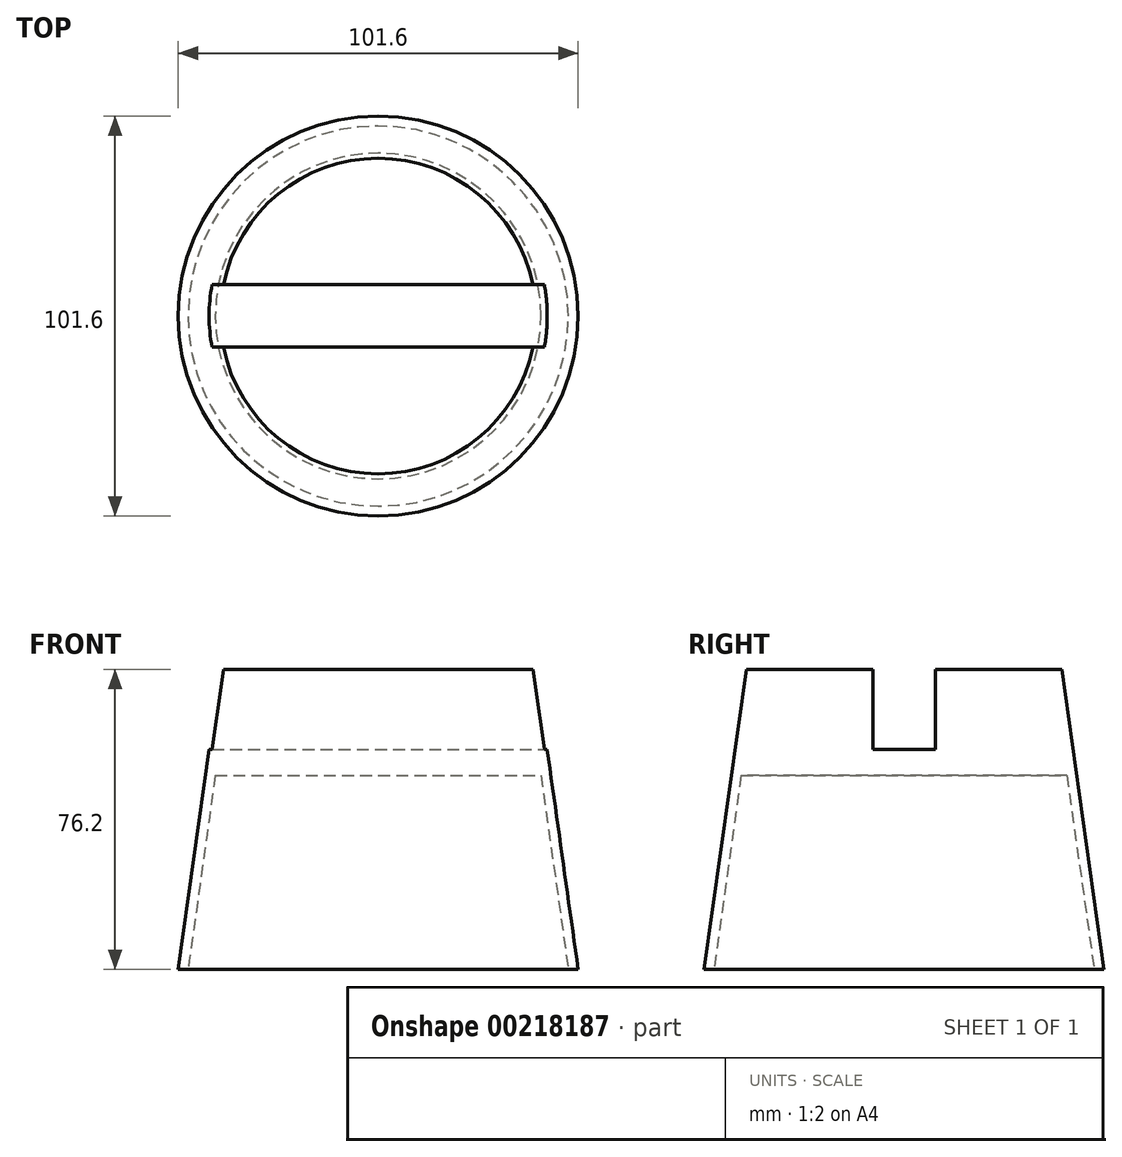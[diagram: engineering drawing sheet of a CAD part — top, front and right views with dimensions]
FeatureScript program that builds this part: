
annotation { "Feature Type Name" : "Feature", "Feature Type Description" : "" }
export const myFeature = defineFeature(function(context is Context, id is Id, definition is map)
    precondition{}
    {
        {
            var Q0;
            Q0=qCreatedBy(makeId("Top.planeOp"),FACE);
            var sketch = newSketch(context, id + "F0", { "sketchPlane" : qUnion([Q0])});
            skCircle(sketch, "E0", {"center": v(0, 0) * mm, "radius": 50.8 * mm});
            skSolve(sketch);
        }
        {
            var Q0;
            Q0 = qSketchRegion(id + "F0", true);
            extrude(context, id + "F1", {"entities" : qUnion([Q0]), "depth" : 76.2 * mm, "hasDraft" : true, "draftAngle" : 8 * degree, "draftPullDirection" : true});
        }
        {
            var Q0;
            Q0=makeQuery(id+"F1.opExtrude","CAP_FACE",FACE,{"disambiguationData":[OSD([sQuery(id+"F0.wireOp",EDGE,"E0")])],"isStart":false});
            var sketch = newSketch(context, id + "F2", { "sketchPlane" : qUnion([Q0])});
            skLineSegment(sketch, "E1.bottom", {"start": v(-63.5, -7.94) * mm, "end": v(63.5, -7.94) * mm});
            skLineSegment(sketch, "E1.top", {"start": v(-63.5, 7.94) * mm, "end": v(63.5, 7.94) * mm});
            skLineSegment(sketch, "E1.left", {"start": v(-63.5, -7.94) * mm, "end": v(-63.5, 7.94) * mm});
            skLineSegment(sketch, "E1.right", {"start": v(63.5, -7.94) * mm, "end": v(63.5, 7.94) * mm});
            skPoint(sketch, "E2", {"position": v(0, 7.94) * mm});
            skPoint(sketch, "E3", {"position": v(0, -7.94) * mm});
            skPoint(sketch, "E4", {"position": v(-63.5, 0) * mm});
            skPoint(sketch, "E5", {"position": v(63.5, 0) * mm});
            skLineSegment(sketch, "E6", {"start": v(40.1, 0) * mm, "end": v(-40.1, 0) * mm, "construction": true});
            skLineSegment(sketch, "E7", {"start": v(0, 40.1) * mm, "end": v(0, -40.1) * mm, "construction": true});
            skSolve(sketch);
        }
        {
            var Q0;
            Q0 = qSketchRegion(id + "F2", true);
            extrude(context, id + "F3", {"entities" : qUnion([Q0]), "operationType" : NewBodyOperationType.REMOVE, "oppositeDirection" : true, "depth" : 20.32 * mm});
        }
        {
            var Q0;
            Q0=makeQuery(id+"F1.opExtrude","CAP_FACE",FACE,{"disambiguationData":[OSD([sQuery(id+"F0.wireOp",EDGE,"E0")])],"isStart":true});
            var sketch = newSketch(context, id + "F4", { "sketchPlane" : qUnion([Q0])});
            skCircle(sketch, "E8", {"center": v(0, 0) * mm, "radius": 48.3 * mm});
            skSolve(sketch);
        }
        {
            var Q0;
            Q0=makeQuery(id+"F4.imprint","IMPRINT",FACE,{"disambiguationData":[TD([[makeQuery(id+"F4.imprint","IMPRINT",EDGE,{"derivedFrom":sQuery(id+"F4.wireOp",EDGE,"E8")}),1.0]])]});
            extrude(context, id + "F5", {"entities" : qUnion([Q0]), "operationType" : NewBodyOperationType.REMOVE, "oppositeDirection" : true, "depth" : 49.28 * mm, "hasDraft" : true, "draftAngle" : 8 * degree, "draftPullDirection" : true});
        }
    });
